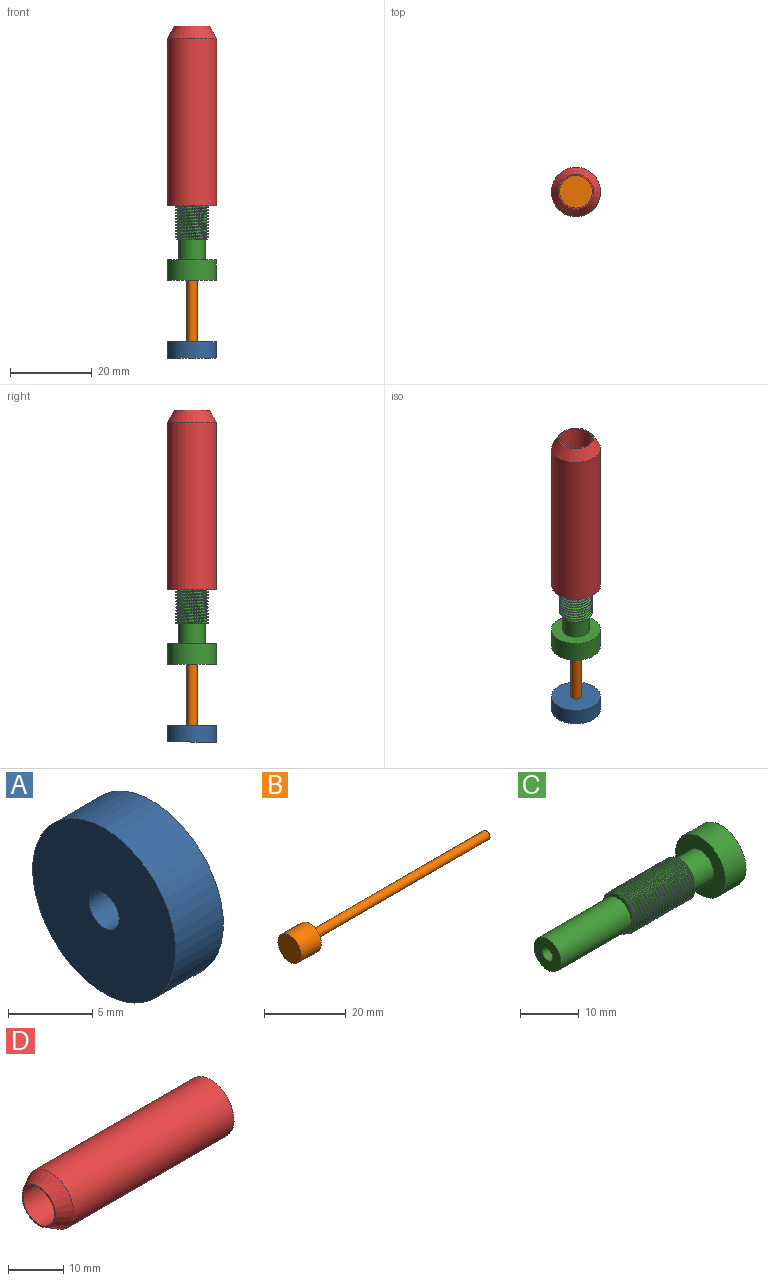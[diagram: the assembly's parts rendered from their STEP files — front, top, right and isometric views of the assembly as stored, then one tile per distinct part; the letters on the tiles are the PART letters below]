
ASSEMBLY  parts=4 mates=3
PART A: 4 faces, bbox 4x12x12 mm
  f0: cylinder r=6mm len=12mm, axis (-1,0,0), area 150.8mm2, adj f1,f3
  f1: plane 12x12mm, normal (-1,0,0), area 108.2mm2, adj f0,f2
  f2: cylinder r=1.25mm len=4mm, axis (-1,0,0), area 31.4mm2, adj f1,f3
  f3: plane 12x12mm, normal (1,0,0), area 108.2mm2, adj f0,f2
PART B: 5 faces, bbox 68x8x8 mm
  f0: plane 8x8mm, normal (-1,0,0), area 50.3mm2, adj f4
  f1: plane 2.5x2.5mm, normal (1,0,0), area 4.9mm2, adj f2
  f2: cylinder r=1.25mm len=61mm, axis (-1,0,0), area 479.1mm2, adj f1,f3
  f3: plane 8x8mm, normal (1,0,0), area 45.4mm2, adj f2,f4
  f4: cylinder r=4mm len=8mm, axis (-1,0,0), area 175.9mm2, adj f0,f3
PART C: 17 faces, bbox 42.2x12.2x12.2 mm
  f0: plane 8.16x7.29mm, normal (1,0,0), area 11.4mm2, adj f1,f7,f8,f11,f12,f13,f14,f15
  f1: cylinder r=4mm len=15mm, axis (-1,0,0), area 8.3mm2, adj f0,f9,f12,f16
  f2: plane 6.5x6.5mm, normal (-1,0,0), area 28.3mm2, adj f3,f10
  f3: cylinder r=1.25mm len=42mm, axis (-1,0,0), area 329.9mm2, adj f2,f4
  f4: plane 12x12mm, normal (1,0,0), area 108.2mm2, adj f3,f5
  f5: cylinder r=6mm len=12mm, axis (-1,0,0), area 188.5mm2, adj f4,f6
  f6: plane 12x12mm, normal (-1,0,0), area 79.9mm2, adj f5,f7
  f7: cylinder r=3.25mm len=6.5mm, axis (-1,0,0), area 102.1mm2, adj f0,f6
  f8: cylinder r=4mm len=15mm, axis (-1,0,0), area 8.3mm2, adj f0,f9,f13,f15
  f9: plane 8.16x7.29mm, normal (-1,0,0), area 11.4mm2, adj f1,f8,f10,f11,f12,f13,f14,f15
  f10: cylinder r=3.25mm len=17mm, axis (-1,0,0), area 347.1mm2, adj f2,f9
  f11: bspline ~15.69x8.3mm, area 47.1mm2, adj f0,f9,f12,f13
  f12: bspline ~15.73x9.24mm, area 112.1mm2, adj f0,f1,f9,f11
  f13: bspline ~15.48x9.24mm, area 111.8mm2, adj f0,f8,f9,f11
  f14: bspline ~15.69x8.3mm, area 47.1mm2, adj f0,f9,f15,f16
  f15: bspline ~15.73x9.24mm, area 112.1mm2, adj f0,f8,f9,f14
  f16: bspline ~15.48x9.24mm, area 111.8mm2, adj f0,f1,f9,f14
PART D: 16 faces, bbox 44.5x12.2x12.2 mm
  f0: plane 12.17x12.17mm, normal (1,0,0), area 67.5mm2, adj f1,f8,f9,f10,f11,f12,f13,f14
  f1: cylinder r=6mm len=41.06mm, axis (-1,0,0), area 1547.8mm2, adj f0,f2
  f2: cone r=6mm half-angle=30deg, axis (1,0,0), area 110mm2, adj f1,f3
  f3: plane 8.6x8.6mm, normal (-1,0,0), area 7.8mm2, adj f2,f4
  f4: cylinder r=4mm len=22mm, axis (-1,0,0), area 552.9mm2, adj f3,f5
  f5: plane 9.5x9.5mm, normal (1,0,0), area 20.6mm2, adj f4,f6
  f6: cylinder r=4.75mm len=9.5mm, axis (-1,0,0), area 59.7mm2, adj f5,f7
  f7: plane 9.67x9.67mm, normal (-1,0,0), area 25.3mm2, adj f6,f8,f9,f10,f11,f12,f13,f14
  f8: bspline ~20.48x9.31mm, area 148.6mm2, adj f0,f7,f10,f14
  f9: bspline ~20.73x9.31mm, area 151.4mm2, adj f0,f7,f10,f15
  f10: bspline ~20.59x9.39mm, area 36.4mm2, adj f0,f7,f8,f9
  f11: bspline ~20.48x9.31mm, area 148.6mm2, adj f0,f7,f13,f15
  f12: bspline ~20.73x9.31mm, area 151.4mm2, adj f0,f7,f13,f14
  f13: bspline ~20.59x9.39mm, area 36.4mm2, adj f0,f7,f11,f12
  f14: cylinder r=3.62mm len=20mm, axis (1,0,0), area 156.6mm2, adj f0,f7,f8,f12
  f15: cylinder r=3.62mm len=20mm, axis (1,0,0), area 156.6mm2, adj f0,f7,f9,f11
PLACE A rot(axis=(0.68,0.26,-0.68),150.7deg) t=(0,0,-4.75)mm
PLACE B rot(axis=(0.68,0.26,-0.68),150.7deg) t=(0,0,-4.75)mm
PLACE C rot(axis=(-0.48,0.73,0.48),107.8deg) t=(0,0,-4.75)mm
PLACE D rot(axis=(0,1,0),90deg) t=(0,0,8.47)mm
MATE fastened B.f2 <-> A.f0  axis (0,0,-1) through (0,0,-57.75)mm
MATE cylindrical C.f1 <-> D.f1  axis (0,0,1) through (0,0,-33.75)mm
MATE cylindrical C.f1 <-> A.f0  axis (0,0,-1) through (0,0,-38.75)mm
